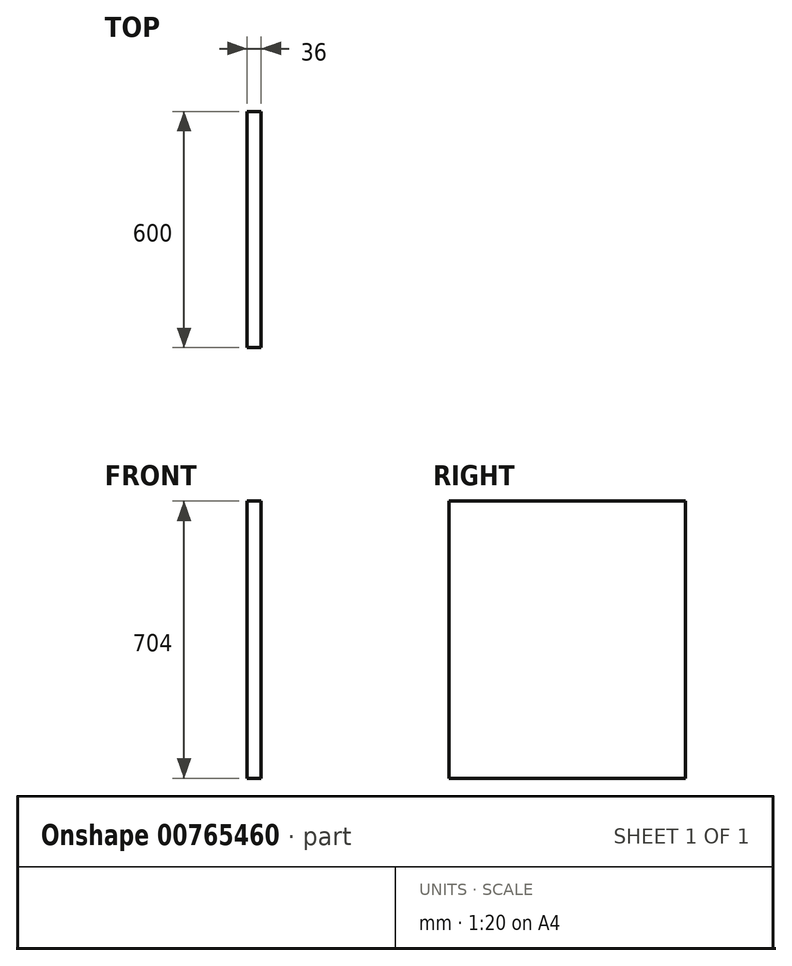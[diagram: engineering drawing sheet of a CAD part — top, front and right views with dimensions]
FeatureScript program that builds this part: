
annotation { "Feature Type Name" : "Feature", "Feature Type Description" : "" }
export const myFeature = defineFeature(function(context is Context, id is Id, definition is map)
    precondition{}
    {
        {
            var Q0;
            Q0=qCreatedBy(makeId("Right.planeOp"),FACE);
            var sketch = newSketch(context, id + "F0", { "sketchPlane" : qUnion([Q0])});
            skLineSegment(sketch, "E0.bottom", {"start": v(-300, -352) * mm, "end": v(300, -352) * mm});
            skLineSegment(sketch, "E0.top", {"start": v(-300, 352) * mm, "end": v(300, 352) * mm});
            skLineSegment(sketch, "E0.left", {"start": v(-300, -352) * mm, "end": v(-300, 352) * mm});
            skLineSegment(sketch, "E0.right", {"start": v(300, -352) * mm, "end": v(300, 352) * mm});
            skPoint(sketch, "E0.middle", {"position": v(0, 0) * mm});
            skSolve(sketch);
        }
        {
            var Q0;
            Q0 = qSketchRegion(id + "F0", true);
            extrude(context, id + "F1", {"entities" : qUnion([Q0]), "depth" : 36 * mm, "offsetDistance" : 25 * mm});
        }
    });
